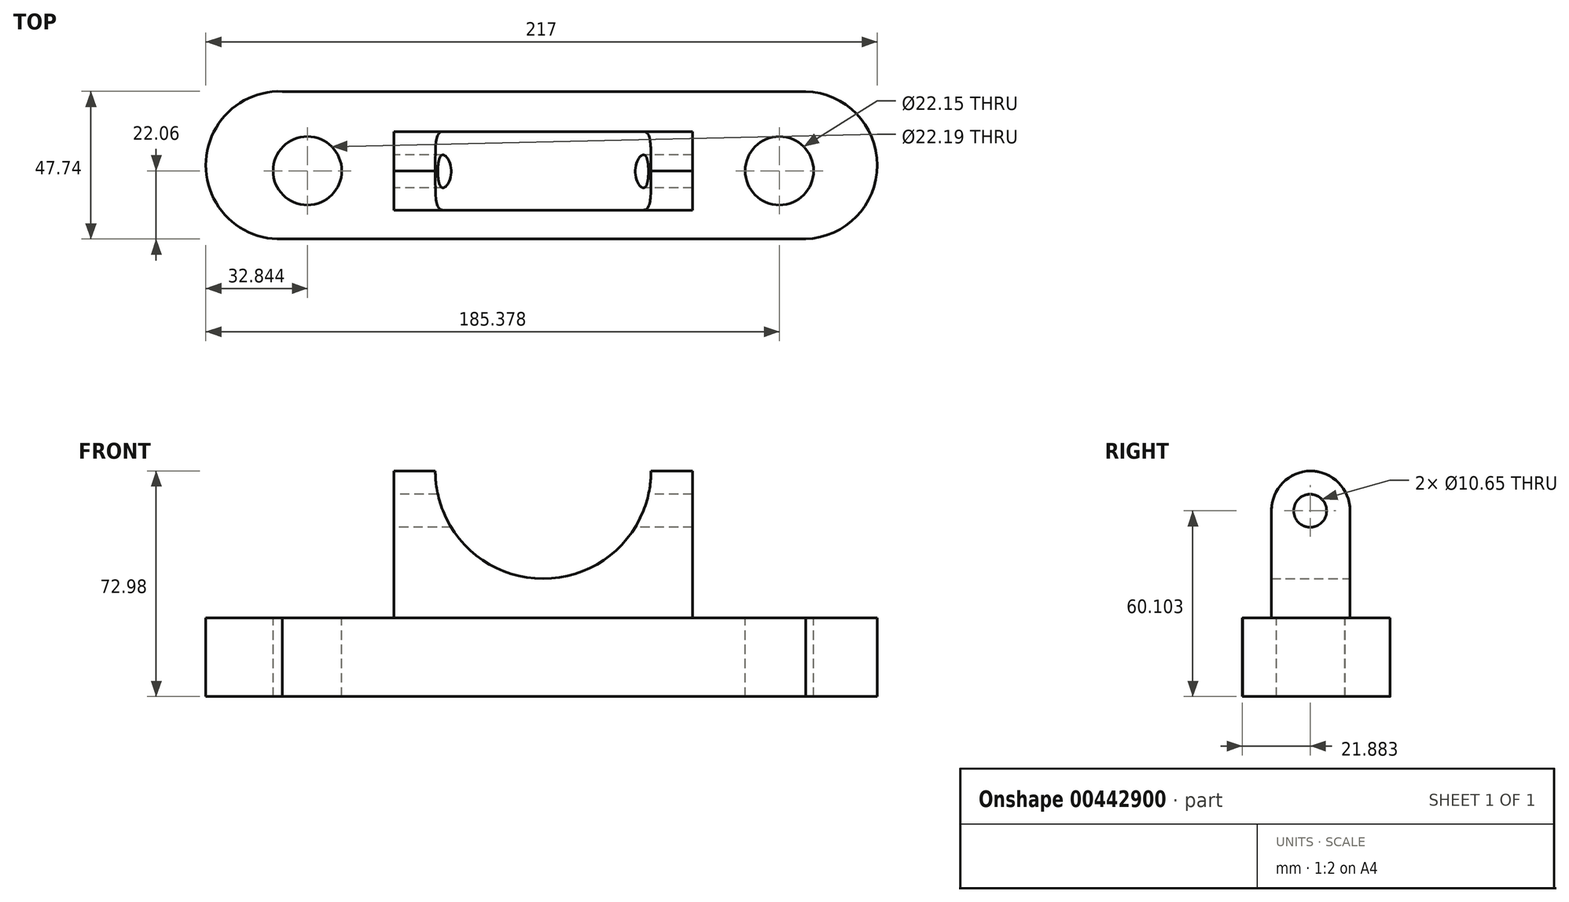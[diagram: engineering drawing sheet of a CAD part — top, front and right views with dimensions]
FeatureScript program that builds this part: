
annotation { "Feature Type Name" : "Feature", "Feature Type Description" : "" }
export const myFeature = defineFeature(function(context is Context, id is Id, definition is map)
    precondition{}
    {
        {
            var Q0;
            Q0=qCreatedBy(makeId("Top.planeOp"),FACE);
            var sketch = newSketch(context, id + "F0", { "sketchPlane" : qUnion([Q0])});
            skLineSegment(sketch, "E0.bottom", {"start": v(-84.34, 25.66) * mm, "end": v(84.82, 25.66) * mm});
            skLineSegment(sketch, "E0.top", {"start": v(-84.34, -22.05) * mm, "end": v(84.82, -22.05) * mm});
            skLineSegment(sketch, "E0.left", {"start": v(-84.34, 25.66) * mm, "end": v(-84.34, -22.05) * mm});
            skLineSegment(sketch, "E0.right", {"start": v(84.82, 25.66) * mm, "end": v(84.82, -22.05) * mm});
            skArc(sketch, "E1", {"start": v(-84.34, 25.66) * mm, "mid": v(-109.03, 1.8) * mm, "end": v(-84.34, -22.05) * mm});
            skPoint(sketch, "E1.third.point", {"position": v(-108.68, -2.29) * mm});
            skArc(sketch, "E2", {"start": v(83.38, -22.05) * mm, "mid": v(107.97, 1.8) * mm, "end": v(83.38, 25.66) * mm});
            skPoint(sketch, "E2.third.point", {"position": v(64.58, -11.93) * mm});
            skSolve(sketch);
        }
        {
            var Q0;
            Q0=makeQuery(id+"F0.imprint","IMPRINT",FACE,{"disambiguationData":[TD([[makeQuery(id+"F0.imprint","IMPRINT",EDGE,{"derivedFrom":sQuery(id+"F0.wireOp",EDGE,"E0.left")}),-1.0]])]});
            var Q1;
            {var subQ5=sQuery(id+"F0.wireOp",EDGE,"E0.left");Q1=makeQuery(id+"F0.imprint","IMPRINT",FACE,{"disambiguationData":[TD([[makeQuery(id+"F0.imprint","IMPRINT",EDGE,{"derivedFrom":subQ5}),1.0]])]});}
            var Q2;
            {var subQ0=sQuery(id+"F0.wireOp",EDGE,"E0.right");Q2=makeQuery(id+"F0.imprint","IMPRINT",FACE,{"disambiguationData":[TD([[makeQuery(id+"F0.imprint","IMPRINT",EDGE,{"derivedFrom":subQ0}),1.0]])]});}
            extrude(context, id + "F1", {"entities" : qUnion([Q0, Q1, Q2]), "depth" : 25.4 * mm});
        }
        {
            var Q0;
            Q0=makeQuery(id+"F1.opExtrude","CAP_FACE",FACE,{"disambiguationData":[OSD([sQuery(id+"F0.wireOp",EDGE,"E0.bottom"),sQuery(id+"F0.wireOp",EDGE,"E0.top"),sQuery(id+"F0.wireOp",EDGE,"E1"),sQuery(id+"F0.wireOp",EDGE,"E2")])],"isStart":false});
            var sketch = newSketch(context, id + "F2", { "sketchPlane" : qUnion([Q0])});
            skCircle(sketch, "E3", {"center": v(-76.19, 0) * mm, "radius": 11.1 * mm});
            skCircle(sketch, "E4", {"center": v(76.35, 0) * mm, "radius": 11.08 * mm});
            skSolve(sketch);
        }
        {
            var Q0;
            Q0=makeQuery(id+"F2.imprint","IMPRINT",FACE,{"disambiguationData":[TD([[makeQuery(id+"F2.imprint","IMPRINT",EDGE,{"derivedFrom":sQuery(id+"F2.wireOp",EDGE,"E3")}),1.0]])]});
            var Q1;
            Q1=makeQuery(id+"F2.imprint","IMPRINT",FACE,{"disambiguationData":[TD([[makeQuery(id+"F2.imprint","IMPRINT",EDGE,{"derivedFrom":sQuery(id+"F2.wireOp",EDGE,"E4")}),1.0]])]});
            extrude(context, id + "F3", {"entities" : qUnion([Q0, Q1]), "operationType" : NewBodyOperationType.REMOVE, "oppositeDirection" : true, "depth" : 51.82 * mm});
        }
        {
            var Q0;
            Q0=qCreatedBy(makeId("Front.planeOp"),FACE);
            var sketch = newSketch(context, id + "F4", { "sketchPlane" : qUnion([Q0])});
            skLineSegment(sketch, "E5.bottom", {"start": v(-48.25, 72.98) * mm, "end": v(-34.86, 72.98) * mm});
            skLineSegment(sketch, "E5.left", {"start": v(-48.25, 72.98) * mm, "end": v(-48.25, 0) * mm});
            skLineSegment(sketch, "E5.right", {"start": v(48.25, 72.98) * mm, "end": v(48.25, 0) * mm});
            skPoint(sketch, "E5.middle", {"position": v(0, 0) * mm});
            skLineSegment(sketch, "E6", {"start": v(-48.25, 0) * mm, "end": v(48.25, 0) * mm});
            skPoint(sketch, "E5.top.end.orphan", {"position": v(48.25, -72.98) * mm});
            skPoint(sketch, "E5.top.start.orphan", {"position": v(-48.25, -72.98) * mm});
            skArc(sketch, "E7", {"start": v(-34.86, 72.98) * mm, "mid": v(0, 38.12) * mm, "end": v(34.86, 72.98) * mm});
            skLineSegment(sketch, "E8.trimOffspring", {"start": v(34.86, 72.98) * mm, "end": v(48.25, 72.98) * mm});
            skSolve(sketch);
        }
        {
            var Q0;
            Q0=makeQuery(id+"F4.imprint","IMPRINT",FACE,{"disambiguationData":[TD([[makeQuery(id+"F4.imprint","IMPRINT",EDGE,{"derivedFrom":sQuery(id+"F4.wireOp",EDGE,"E5.bottom")}),-1.0]])]});
            extrude(context, id + "F5", {"entities" : qUnion([Q0]), "operationType" : NewBodyOperationType.ADD, "depth" : 25.4 * mm, "symmetric" : true});
        }
        {
            var Q0;
            Q0=makeQuery(id+"F5.opExtrude","CAP_EDGE",EDGE,{"disambiguationData":[OSD([sQuery(id+"F4.wireOp",EDGE,"E5.bottom")])],"isStart":false});
            var Q1;
            Q1=makeQuery(id+"F5.opExtrude","CAP_EDGE",EDGE,{"disambiguationData":[OSD([sQuery(id+"F4.wireOp",EDGE,"E5.bottom")])],"isStart":true});
            var Q2;
            Q2=makeQuery(id+"F5.opExtrude","CAP_EDGE",EDGE,{"disambiguationData":[OSD([sQuery(id+"F4.wireOp",EDGE,"E8.trimOffspring")])],"isStart":true});
            var Q3;
            Q3=makeQuery(id+"F5.opExtrude","CAP_EDGE",EDGE,{"disambiguationData":[OSD([sQuery(id+"F4.wireOp",EDGE,"E8.trimOffspring")])],"isStart":false});
            fillet(context, id + "F6", {"entities" : qUnion([Q0, Q1, Q2, Q3]), "radius" : 12.88 * mm, "tangentPropagation" : true, "allowEdgeOverflow" : false});
        }
        {
            var Q0;
            Q0=makeQuery(id+"F5.opExtrude","SWEPT_FACE",FACE,{"disambiguationData":[OSD([sQuery(id+"F4.wireOp",EDGE,"E5.left")])]});
            var sketch = newSketch(context, id + "F7", { "sketchPlane" : qUnion([Q0])});
            skCircle(sketch, "E9", {"center": v(0.18, 60.1) * mm, "radius": 5.32 * mm});
            skSolve(sketch);
        }
        {
            var Q0;
            Q0 = qSketchRegion(id + "F7", true);
            extrude(context, id + "F8", {"entities" : qUnion([Q0]), "operationType" : NewBodyOperationType.REMOVE, "oppositeDirection" : true, "depth" : 189.48 * mm});
        }
    });
